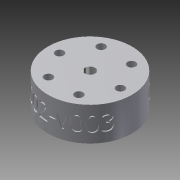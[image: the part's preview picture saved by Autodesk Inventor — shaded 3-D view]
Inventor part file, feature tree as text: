
AUTODESK INVENTOR PART (.ipt)
format: ipt  version: 2014 (Build 180170000, 170)  size: 3,039,232 bytes
history: native  units: mm
features: other x7, extrude x5, sketch x4, boolean_combine x1, plane x1, hole x1
ambient origin geometry x8: Origin, YZ Plane, XZ Plane, XY Plane, X Axis, Y Axis, Z Axis, Center Point
bodies: Solid1 (feature_tree), Solid3 (feature_tree)
feature tree (19):
  other  "MOT_WindowMotor_262100-3040.ipt"
  extrude  "Extrusion1"  Depth=30.0mm TaperAngle=0.0deg
  boolean_combine  "Combine2"
  other  "Thicken adapter hole"
  extrude  "Extrusion2"  Depth=10.0mm
  extrude  "Extrusion for middle hole"  Depth=20.0mm
  other  "Thicken Center Hole"
  extrude  "Extrusion for bolt holes"  Depth=35.0mm TaperAngle=0.0deg
  extrude  "Extrusion10"  Depth=35.0mm
  plane  "Work Plane1"
  other  "Emboss of part number"
  sketch  "Sketch1"  dims[d0=70.0mm d1=30.0mm d2=0.0mm]
  other  "Solid1::MOT_WindowMotor_262100-3040.ipt"
  other  "TaggingFeature2"
  other  "Smooth Base"
  hole  "Hole to view fit"  [1 undecoded]
  sketch  "Sketch14"  dims[d7=10.0mm d8=0.225mm d9=0.5mm]
  sketch  "Sketch for bolt holes"  dims[d10=70.0mm d11=20.0mm]
  sketch  "Sketch for part number"  dims[d12=2.0mm d13=0.0mm d22=3.0mm d23=0.0mm d44=0.2mm d45=0.01mm d66=6.858mm d67=25.4mm d68=60.0mm d70=360.0deg d72=30.0mm d73=0.0mm d74=11.3665mm d75=60.0mm d77=360.0deg d79=4.5mm d80=0.0mm d81=35.0mm d82=1.0mm d83=0.0mm d90=7.0mm]
note: 1 required parameter value undecoded (feature->parameter linkage not recoverable at this tier; creation-order binding heuristic only, values carry confidence <= 0.55)
